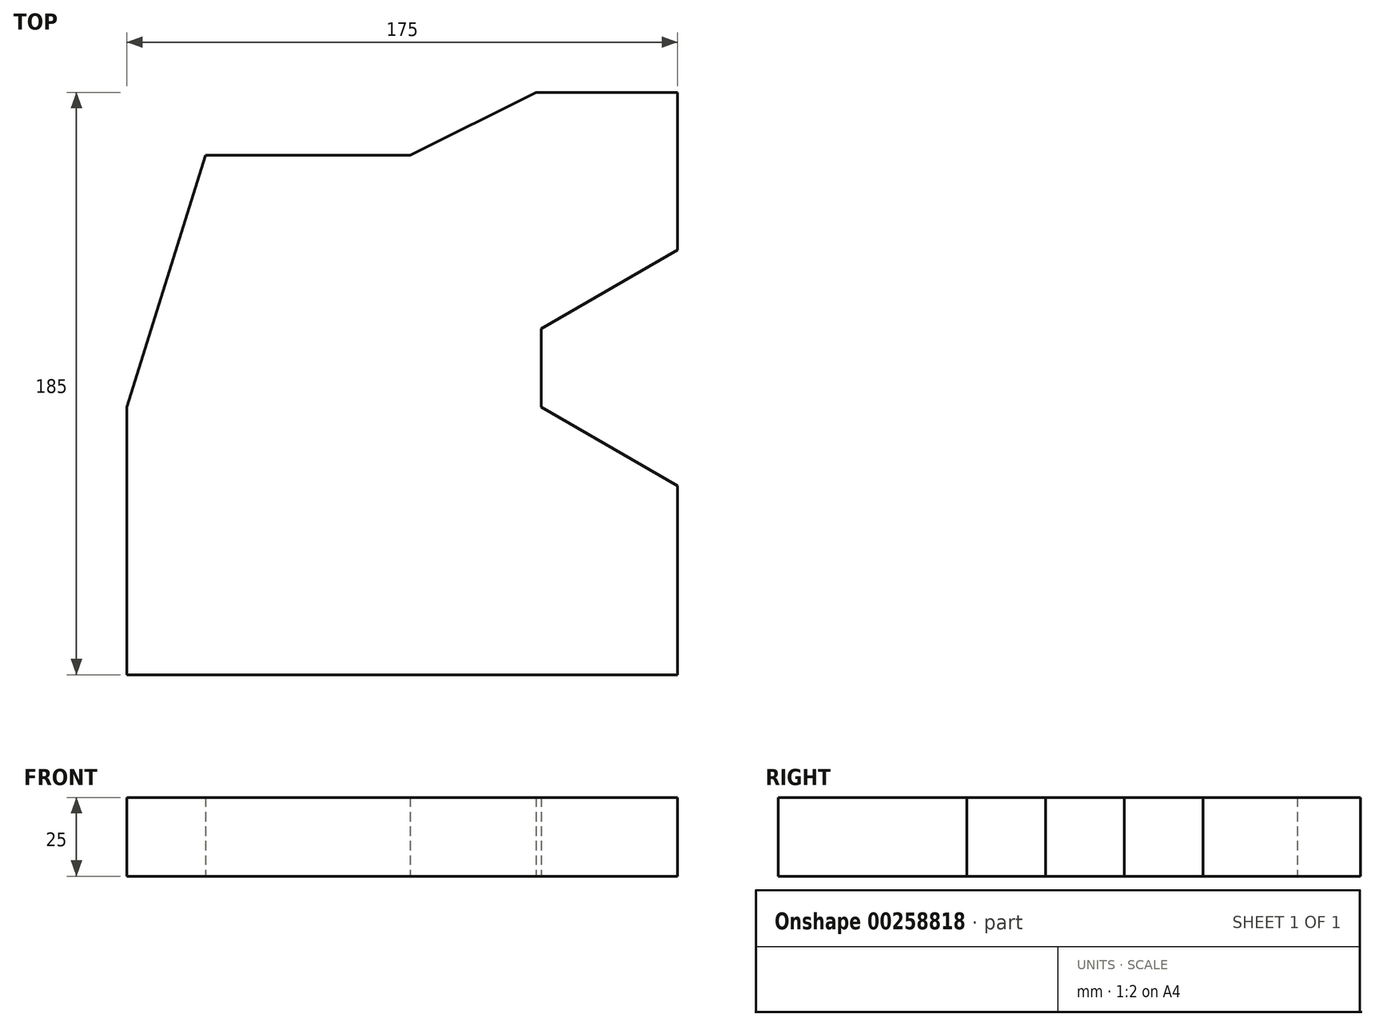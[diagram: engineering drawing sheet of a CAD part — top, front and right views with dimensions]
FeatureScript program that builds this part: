
annotation { "Feature Type Name" : "Feature", "Feature Type Description" : "" }
export const myFeature = defineFeature(function(context is Context, id is Id, definition is map)
    precondition{}
    {
        {
            var Q0;
            Q0=qCreatedBy(makeId("Top.planeOp"),FACE);
            var sketch = newSketch(context, id + "F0", { "sketchPlane" : qUnion([Q0])});
            skLineSegment(sketch, "E0", {"start": v(76.3, -73.25) * mm, "end": v(-98.7, -73.25) * mm});
            skLineSegment(sketch, "E1", {"start": v(-98.7, -73.25) * mm, "end": v(-98.7, 11.75) * mm});
            skLineSegment(sketch, "E2", {"start": v(-98.7, 11.75) * mm, "end": v(-73.7, 91.75) * mm});
            skLineSegment(sketch, "E3", {"start": v(-73.7, 91.75) * mm, "end": v(-8.7, 91.75) * mm});
            skLineSegment(sketch, "E4", {"start": v(-8.7, 91.75) * mm, "end": v(31.3, 111.75) * mm});
            skLineSegment(sketch, "E5", {"start": v(31.3, 111.75) * mm, "end": v(76.3, 111.75) * mm});
            skLineSegment(sketch, "E6", {"start": v(76.3, 111.75) * mm, "end": v(76.3, 61.75) * mm});
            skLineSegment(sketch, "E7", {"start": v(76.3, 61.75) * mm, "end": v(32.99, 36.75) * mm});
            skLineSegment(sketch, "E8", {"start": v(32.99, 36.75) * mm, "end": v(32.99, 11.75) * mm});
            skLineSegment(sketch, "E9", {"start": v(76.3, -73.25) * mm, "end": v(76.3, -13.25) * mm});
            skLineSegment(sketch, "E10", {"start": v(32.99, 11.75) * mm, "end": v(76.3, -13.25) * mm});
            skLineSegment(sketch, "E11", {"start": v(32.99, 36.75) * mm, "end": v(75.04, 36.75) * mm});
            skLineSegment(sketch, "E12", {"start": v(32.99, 11.75) * mm, "end": v(71.68, 11.75) * mm});
            skSolve(sketch);
        }
        {
            var Q0;
            Q0 = qSketchRegion(id + "F0", true);
            extrude(context, id + "F1", {"entities" : qUnion([Q0]), "depth" : 25 * mm});
        }
    });
